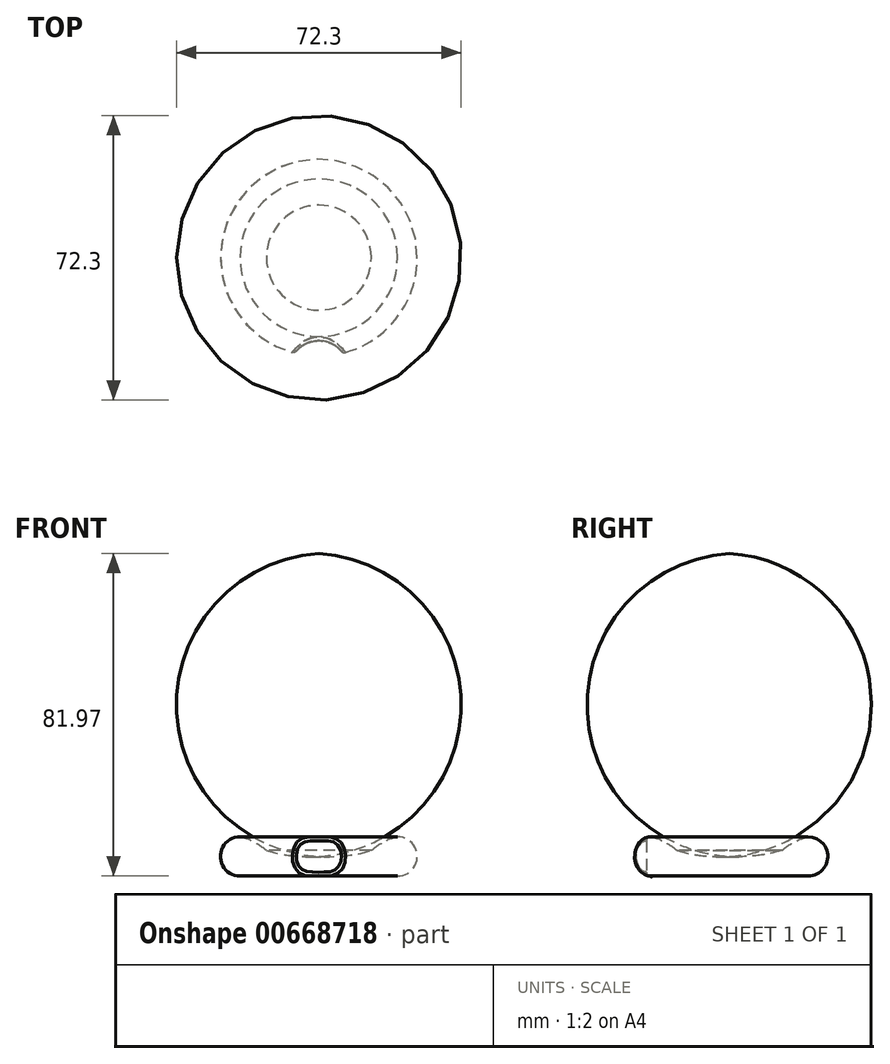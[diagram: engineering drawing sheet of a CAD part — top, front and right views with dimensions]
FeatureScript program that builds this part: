
annotation { "Feature Type Name" : "Feature", "Feature Type Description" : "" }
export const myFeature = defineFeature(function(context is Context, id is Id, definition is map)
    precondition{}
    {
        {
            var Q0;
            Q0=qCreatedBy(makeId("Front.planeOp"),FACE);
            var sketch = newSketch(context, id + "F0", { "sketchPlane" : qUnion([Q0])});
            skLineSegment(sketch, "E0", {"start": v(0, 0) * mm, "end": v(20, 0) * mm});
            skArc(sketch, "E1", {"start": v(20, 0) * mm, "mid": v(25, 5) * mm, "end": v(20, 10) * mm});
            skArc(sketch, "E2", {"start": v(20, 10) * mm, "mid": v(16.47, 8.64) * mm, "end": v(13.34, 6.5) * mm});
            skArc(sketch, "E3", {"start": v(0, 5) * mm, "mid": v(6.73, 5.17) * mm, "end": v(13.34, 6.5) * mm});
            skLineSegment(sketch, "E4", {"start": v(0, 5) * mm, "end": v(0, 0) * mm});
            skSolve(sketch);
        }
        {
            var Q0;
            Q0=makeQuery(id+"F0.imprint","IMPRINT",FACE,{"disambiguationData":[TD([[makeQuery(id+"F0.imprint","IMPRINT",EDGE,{"derivedFrom":sQuery(id+"F0.wireOp",EDGE,"E0")}),1.0]])]});
            var Q1;
            Q1=sQuery(id+"F0.wireOp",EDGE,"E4");
            revolve(context, id + "F1", {"entities" : qUnion([Q0]), "axis" : qUnion([Q1]), "revolveType" : RevolveType.FULL});
        }
        {
            var Q0;
            Q0=qCreatedBy(makeId("Top.planeOp"),FACE);
            var sketch = newSketch(context, id + "F2", { "sketchPlane" : qUnion([Q0])});
            skCircle(sketch, "E5", {"center": v(0, -28.6) * mm, "radius": 7.5 * mm});
            skSolve(sketch);
        }
        {
            var Q0;
            Q0 = qSketchRegion(id + "F2", true);
            extrude(context, id + "F3", {"entities" : qUnion([Q0]), "operationType" : NewBodyOperationType.REMOVE, "endBound" : BoundingType.THROUGH_ALL, "depth" : 25 * mm, "offsetDistance" : 25 * mm});
        }
        {
            var Q0;
            Q0=makeQuery(id+"F3.boolean.opBoolean","COPY",FACE,{"derivedFrom":makeQuery(id+"F3.opExtrude","SWEPT_FACE",FACE,{"disambiguationData":[OSD([sQuery(id+"F2.wireOp",EDGE,"E5")])]})});
            fillet(context, id + "F4", {"entities" : qUnion([Q0]), "radius" : 1 * mm, "tangentPropagation" : true, "allowEdgeOverflow" : false});
        }
    });
